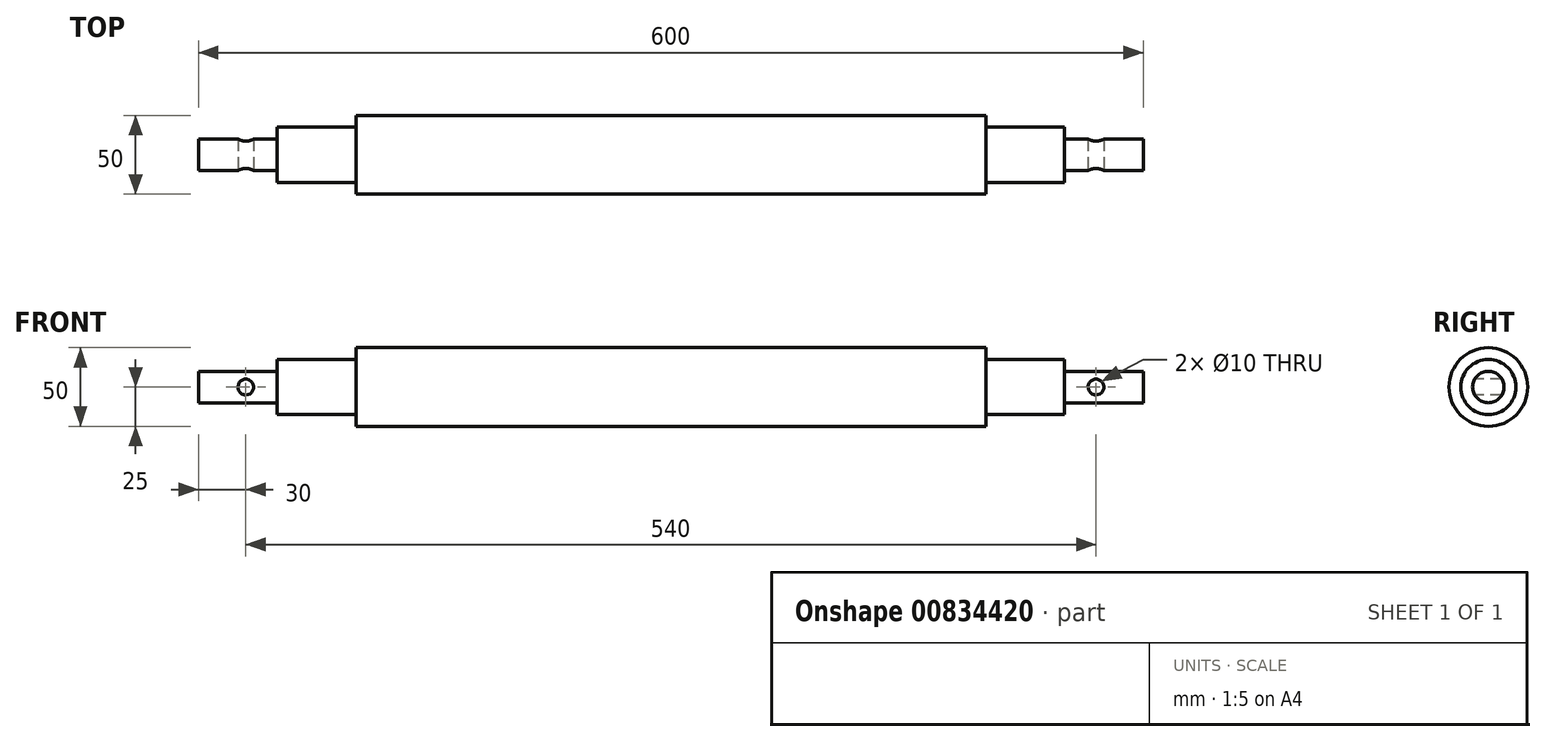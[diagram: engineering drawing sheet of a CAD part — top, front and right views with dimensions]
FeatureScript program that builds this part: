
annotation { "Feature Type Name" : "Feature", "Feature Type Description" : "" }
export const myFeature = defineFeature(function(context is Context, id is Id, definition is map)
    precondition{}
    {
        {
            var Q0;
            Q0=qCreatedBy(makeId("Right.planeOp"),FACE);
            var sketch = newSketch(context, id + "F0", { "sketchPlane" : qUnion([Q0])});
            skCircle(sketch, "E0", {"center": v(0, 0) * mm, "radius": 25 * mm});
            skSolve(sketch);
        }
        {
            var Q0;
            Q0 = qSketchRegion(id + "F0", true);
            extrude(context, id + "F1", {"entities" : qUnion([Q0]), "endBound" : BoundingType.SYMMETRIC, "depth" : 400 * mm, "offsetDistance" : 25 * mm});
        }
        {
            var Q0;
            Q0=makeQuery(id+"F1.opExtrude","CAP_FACE",FACE,{"disambiguationData":[OSD([sQuery(id+"F0.wireOp",EDGE,"E0")])],"isStart":false});
            var sketch = newSketch(context, id + "F2", { "sketchPlane" : qUnion([Q0])});
            skCircle(sketch, "E1", {"center": v(0, 0) * mm, "radius": 10 * mm});
            skSolve(sketch);
        }
        {
            var Q0;
            Q0 = qSketchRegion(id + "F2", true);
            extrude(context, id + "F3", {"entities" : qUnion([Q0]), "operationType" : NewBodyOperationType.ADD, "depth" : 100 * mm, "offsetDistance" : 25 * mm});
        }
        {
            var Q0;
            Q0=makeQuery(id+"F1.opExtrude","CAP_FACE",FACE,{"disambiguationData":[OSD([sQuery(id+"F0.wireOp",EDGE,"E0")])],"isStart":true});
            var sketch = newSketch(context, id + "F4", { "sketchPlane" : qUnion([Q0])});
            skCircle(sketch, "E2", {"center": v(0, 0) * mm, "radius": 10 * mm});
            skSolve(sketch);
        }
        {
            var Q0;
            Q0 = qSketchRegion(id + "F4", true);
            extrude(context, id + "F5", {"entities" : qUnion([Q0]), "operationType" : NewBodyOperationType.ADD, "depth" : 100 * mm, "offsetDistance" : 25 * mm});
        }
        {
            var Q0;
            Q0=qCreatedBy(makeId("Front.planeOp"),FACE);
            var sketch = newSketch(context, id + "F6", { "sketchPlane" : qUnion([Q0])});
            skCircle(sketch, "E3", {"center": v(270, 0) * mm, "radius": 5 * mm});
            skCircle(sketch, "E4", {"center": v(-270, 0) * mm, "radius": 5 * mm});
            skSolve(sketch);
        }
        {
            var Q0;
            Q0 = qSketchRegion(id + "F6", true);
            extrude(context, id + "F7", {"entities" : qUnion([Q0]), "operationType" : NewBodyOperationType.REMOVE, "endBound" : BoundingType.SYMMETRIC, "oppositeDirection" : true, "depth" : 100 * mm, "offsetDistance" : 25 * mm});
        }
        {
            var Q0;
            Q0=makeQuery(id+"F1.opExtrude","CAP_FACE",FACE,{"disambiguationData":[OSD([sQuery(id+"F0.wireOp",EDGE,"E0")])],"isStart":true});
            var sketch = newSketch(context, id + "F8", { "sketchPlane" : qUnion([Q0])});
            skCircle(sketch, "E5", {"center": v(0, 0) * mm, "radius": 17.5 * mm});
            skSolve(sketch);
        }
        {
            var Q0;
            Q0 = qSketchRegion(id + "F8", true);
            extrude(context, id + "F9", {"entities" : qUnion([Q0]), "operationType" : NewBodyOperationType.ADD, "depth" : 50 * mm, "offsetDistance" : 25 * mm});
        }
        {
            var Q0;
            Q0=makeQuery(id+"F1.opExtrude","CAP_FACE",FACE,{"disambiguationData":[OSD([sQuery(id+"F0.wireOp",EDGE,"E0")])],"isStart":false});
            var sketch = newSketch(context, id + "F10", { "sketchPlane" : qUnion([Q0])});
            skCircle(sketch, "E6", {"center": v(0, 0) * mm, "radius": 17.5 * mm});
            skSolve(sketch);
        }
        {
            var Q0;
            Q0 = qSketchRegion(id + "F10", true);
            extrude(context, id + "F11", {"entities" : qUnion([Q0]), "operationType" : NewBodyOperationType.ADD, "depth" : 50 * mm, "offsetDistance" : 25 * mm});
        }
    });
